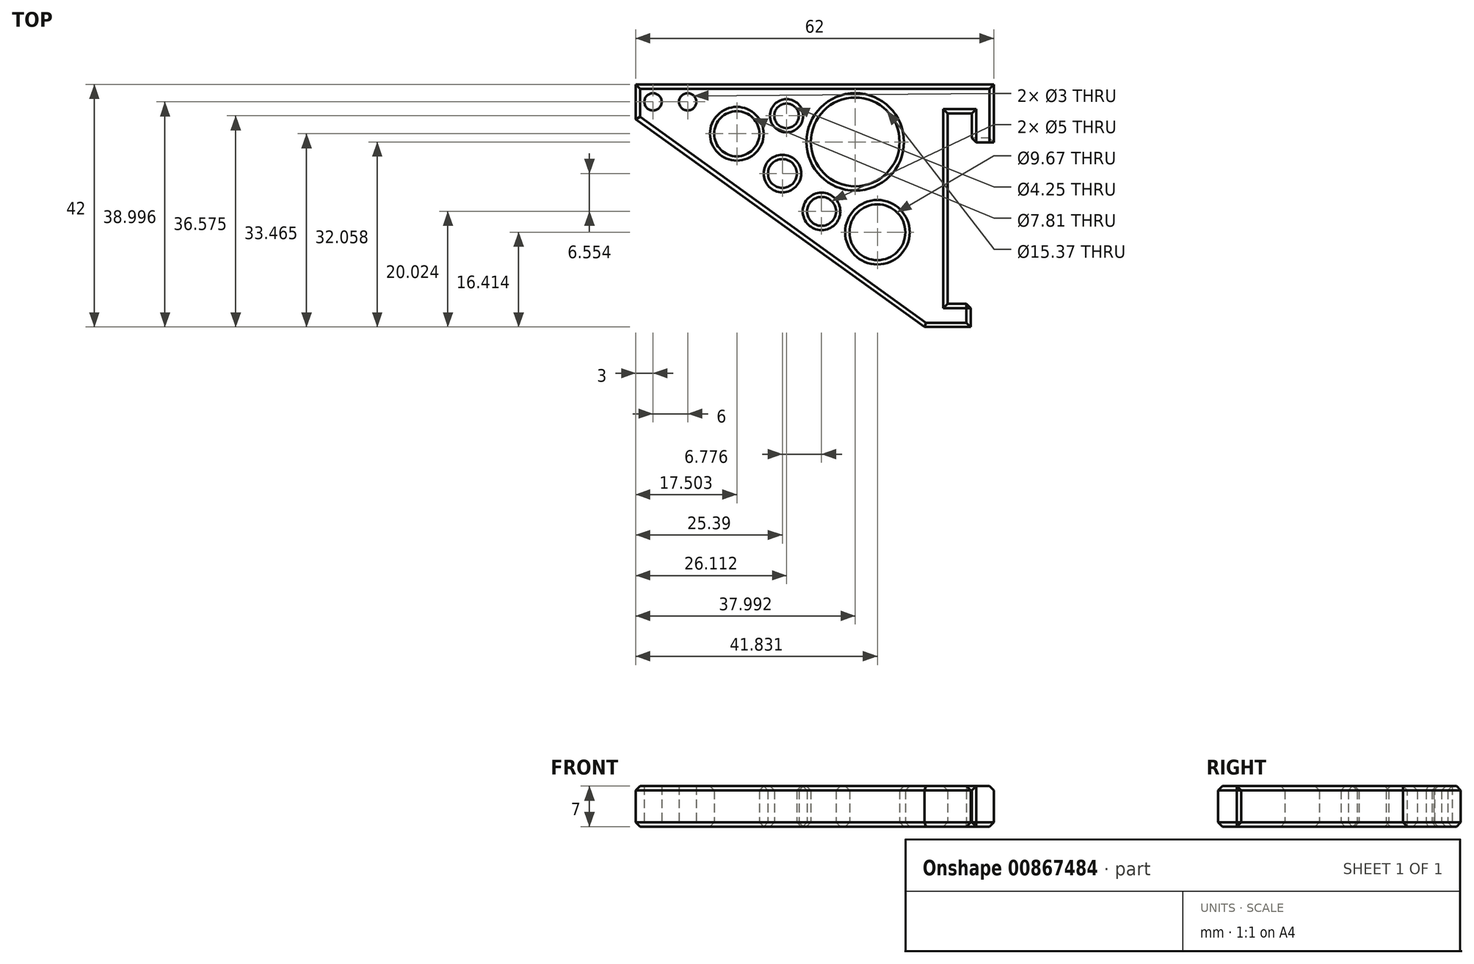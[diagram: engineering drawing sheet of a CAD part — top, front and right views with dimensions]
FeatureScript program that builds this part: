
annotation { "Feature Type Name" : "Feature", "Feature Type Description" : "" }
export const myFeature = defineFeature(function(context is Context, id is Id, definition is map)
    precondition{}
    {
        {
            var Q0;
            Q0=qCreatedBy(makeId("Top.planeOp"),FACE);
            var sketch = newSketch(context, id + "F0", { "sketchPlane" : qUnion([Q0])});
            skLineSegment(sketch, "E0.bottom", {"start": v(0, 15.63) * mm, "end": v(-4, 15.63) * mm});
            skLineSegment(sketch, "E0.top", {"start": v(0, -26.37) * mm, "end": v(-4, -26.37) * mm});
            skLineSegment(sketch, "E0.left", {"start": v(0, 15.63) * mm, "end": v(0, -26.37) * mm});
            skLineSegment(sketch, "E1.bottom", {"start": v(0, 15.63) * mm, "end": v(8, 15.63) * mm});
            skLineSegment(sketch, "E1.top", {"start": v(0, 10.63) * mm, "end": v(8, 10.63) * mm});
            skLineSegment(sketch, "E1.left", {"start": v(0, 15.63) * mm, "end": v(0, 10.63) * mm});
            skLineSegment(sketch, "E1.right", {"start": v(8, 15.63) * mm, "end": v(8, 10.63) * mm});
            skLineSegment(sketch, "E2.bottom", {"start": v(8, 10.63) * mm, "end": v(4.2, 10.63) * mm});
            skLineSegment(sketch, "E2.top", {"start": v(8, 5.63) * mm, "end": v(4.2, 5.63) * mm});
            skLineSegment(sketch, "E2.left", {"start": v(8, 10.63) * mm, "end": v(8, 5.63) * mm});
            skLineSegment(sketch, "E2.right", {"start": v(4.2, 10.63) * mm, "end": v(4.2, 5.63) * mm});
            skLineSegment(sketch, "E3.bottom", {"start": v(0, -26.37) * mm, "end": v(4, -26.37) * mm});
            skLineSegment(sketch, "E3.top", {"start": v(0, -22.37) * mm, "end": v(4, -22.37) * mm});
            skLineSegment(sketch, "E3.left", {"start": v(0, -26.37) * mm, "end": v(0, -22.37) * mm});
            skLineSegment(sketch, "E3.right", {"start": v(4, -26.37) * mm, "end": v(4, -22.37) * mm});
            skLineSegment(sketch, "E4", {"start": v(-4, 15.63) * mm, "end": v(-4, -26.37) * mm});
            skLineSegment(sketch, "E5", {"start": v(-4, 15.63) * mm, "end": v(-54, 15.63) * mm});
            skLineSegment(sketch, "E6", {"start": v(-54, 15.63) * mm, "end": v(-54, 9.63) * mm});
            skLineSegment(sketch, "E7", {"start": v(-54, 9.63) * mm, "end": v(-4, -26.37) * mm});
            skCircle(sketch, "E8", {"center": v(-16, 5.69) * mm, "radius": 7.68 * mm});
            skCircle(sketch, "E9", {"center": v(-36.5, 7.1) * mm, "radius": 3.9 * mm});
            skCircle(sketch, "E10", {"center": v(-27.89, 10.2) * mm, "radius": 2.12 * mm});
            skCircle(sketch, "E11", {"center": v(-28.6, 0.2) * mm, "radius": 2.5 * mm});
            skCircle(sketch, "E12", {"center": v(-12.17, -9.96) * mm, "radius": 4.83 * mm});
            skLineSegment(sketch, "E13.bottom", {"start": v(-54, 15.63) * mm, "end": v(-42, 15.63) * mm});
            skLineSegment(sketch, "E13.top", {"start": v(-54, 9.63) * mm, "end": v(-42, 9.63) * mm});
            skLineSegment(sketch, "E13.right", {"start": v(-42, 15.63) * mm, "end": v(-42, 9.63) * mm});
            skLineSegment(sketch, "E14", {"start": v(-54, 12.63) * mm, "end": v(-51, 12.63) * mm, "construction": true});
            skLineSegment(sketch, "E15", {"start": v(-51, 12.63) * mm, "end": v(-45, 12.63) * mm, "construction": true});
            skLineSegment(sketch, "E16", {"start": v(-45, 12.63) * mm, "end": v(-42, 12.63) * mm, "construction": true});
            skCircle(sketch, "E17", {"center": v(-51, 12.63) * mm, "radius": 1.5 * mm});
            skCircle(sketch, "E18", {"center": v(-45, 12.63) * mm, "radius": 1.5 * mm});
            skCircle(sketch, "E19", {"center": v(-21.83, -6.35) * mm, "radius": 2.5 * mm});
            skSolve(sketch);
        }
        {
            var Q0;
            {var subQ1=sQuery(id+"F0.wireOp",EDGE,"E0.bottom");Q0=makeQuery(id+"F0.imprint","IMPRINT",FACE,{"disambiguationData":[TD([[makeQuery(id+"F0.imprint","IMPRINT",EDGE,{"derivedFrom":subQ1}),1.0]])]});}
            var Q1;
            {var subQ4=sQuery(id+"F0.wireOp",EDGE,"E1.bottom");Q1=makeQuery(id+"F0.imprint","IMPRINT",FACE,{"disambiguationData":[TD([[makeQuery(id+"F0.imprint","IMPRINT",EDGE,{"derivedFrom":subQ4}),-1.0]])]});}
            var Q2;
            Q2=makeQuery(id+"F0.imprint","IMPRINT",FACE,{"disambiguationData":[TD([[makeQuery(id+"F0.imprint","IMPRINT",EDGE,{"derivedFrom":sQuery(id+"F0.wireOp",EDGE,"E2.top")}),-1.0]])]});
            var Q3;
            {var subQ0=sQuery(id+"F0.wireOp",EDGE,"E3.bottom");Q3=makeQuery(id+"F0.imprint","IMPRINT",FACE,{"disambiguationData":[TD([[makeQuery(id+"F0.imprint","IMPRINT",EDGE,{"derivedFrom":subQ0}),1.0]])]});}
            var Q4;
            {var subQ0=sQuery(id+"F0.wireOp",EDGE,"E4");Q4=makeQuery(id+"F0.imprint","IMPRINT",FACE,{"disambiguationData":[TD([[makeQuery(id+"F0.imprint","IMPRINT",EDGE,{"derivedFrom":subQ0}),-1.0]])]});}
            var Q5;
            {var subQ0=sQuery(id+"F0.wireOp",EDGE,"E6");Q5=makeQuery(id+"F0.imprint","IMPRINT",FACE,{"disambiguationData":[TD([[makeQuery(id+"F0.imprint","IMPRINT",EDGE,{"derivedFrom":subQ0}),1.0]])]});}
            extrude(context, id + "F1", {"entities" : qUnion([Q0, Q1, Q2, Q3, Q4, Q5]), "depth" : 7 * mm, "offsetDistance" : 25 * mm});
        }
        {
            var Q0;
            Q0=makeQuery(id+"F1.opExtrude","SWEPT_EDGE",EDGE,{"disambiguationData":[OSD([sQuery(id+"F0.wireOp",EDGE,"E2.top"),sQuery(id+"F0.wireOp",EDGE,"E2.right")])]});
            var Q1;
            Q1=makeQuery(id+"F1.opExtrude","SWEPT_EDGE",EDGE,{"disambiguationData":[OSD([sQuery(id+"F0.wireOp",EDGE,"E3.top"),sQuery(id+"F0.wireOp",EDGE,"E3.right")])]});
            var Q2;
            Q2=makeQuery(id+"F1.opExtrude","CAP_EDGE",EDGE,{"disambiguationData":[OSD([sQuery(id+"F0.wireOp",EDGE,"uG2Vx7Yd-SFKq-mX41-H8Db-6Rk8HB1i1w4M")])],"isStart":true});
            var Q3;
            Q3=makeQuery(id+"F1.opExtrude","CAP_EDGE",EDGE,{"disambiguationData":[OSD([sQuery(id+"F0.wireOp",EDGE,"uG2Vx7Yd-SFKq-mX41-H8Db-6Rk8HB1i1w4M")])],"isStart":false});
            var Q4;
            Q4=makeQuery(id+"F1.opExtrude","CAP_EDGE",EDGE,{"disambiguationData":[OSD([sQuery(id+"F0.wireOp",EDGE,"E12")])],"isStart":true});
            var Q5;
            Q5=makeQuery(id+"F1.opExtrude","CAP_EDGE",EDGE,{"disambiguationData":[OSD([sQuery(id+"F0.wireOp",EDGE,"oTn9qpCm-4VPc-hakh-BUWp-S5fq27Ghi3sC")])],"isStart":true});
            var Q6;
            Q6=makeQuery(id+"F1.opExtrude","CAP_EDGE",EDGE,{"disambiguationData":[OSD([sQuery(id+"F0.wireOp",EDGE,"eH2JkWFH-rGqj-qHwk-75RG-LBSng5KapZW2")])],"isStart":true});
            var Q7;
            Q7=makeQuery(id+"F1.opExtrude","CAP_EDGE",EDGE,{"disambiguationData":[OSD([sQuery(id+"F0.wireOp",EDGE,"WzFQYJBc-jEeU-135c-dLvn-cKav0WjsmrNZ")])],"isStart":true});
            var Q8;
            Q8=makeQuery(id+"F1.opExtrude","CAP_EDGE",EDGE,{"disambiguationData":[OSD([sQuery(id+"F0.wireOp",EDGE,"E11")])],"isStart":true});
            var Q9;
            Q9=makeQuery(id+"F1.opExtrude","CAP_EDGE",EDGE,{"disambiguationData":[OSD([sQuery(id+"F0.wireOp",EDGE,"E9")])],"isStart":false});
            var Q10;
            Q10=makeQuery(id+"F1.opExtrude","CAP_EDGE",EDGE,{"disambiguationData":[OSD([sQuery(id+"F0.wireOp",EDGE,"E9")])],"isStart":true});
            var Q11;
            Q11=makeQuery(id+"F1.opExtrude","CAP_EDGE",EDGE,{"disambiguationData":[OSD([sQuery(id+"F0.wireOp",EDGE,"E10")])],"isStart":true});
            var Q12;
            Q12=makeQuery(id+"F1.opExtrude","CAP_EDGE",EDGE,{"disambiguationData":[OSD([sQuery(id+"F0.wireOp",EDGE,"E8")])],"isStart":true});
            var Q13;
            Q13=makeQuery(id+"F1.opExtrude","CAP_EDGE",EDGE,{"disambiguationData":[OSD([sQuery(id+"F0.wireOp",EDGE,"E0.left")])],"isStart":true});
            var Q14;
            Q14=makeQuery(id+"F1.opExtrude","CAP_EDGE",EDGE,{"disambiguationData":[OSD([sQuery(id+"F0.wireOp",EDGE,"E1.top")])],"isStart":true});
            var Q15;
            Q15=makeQuery(id+"F1.opExtrude","CAP_EDGE",EDGE,{"disambiguationData":[OSD([sQuery(id+"F0.wireOp",EDGE,"E2.right")])],"isStart":true});
            var Q16;
            Q16=makeQuery(id+"F1.opExtrude","CAP_EDGE",EDGE,{"disambiguationData":[OSD([sQuery(id+"F0.wireOp",EDGE,"E2.top")])],"isStart":true});
            var Q17;
            Q17=makeQuery(id+"F1.opExtrude","CAP_EDGE",EDGE,{"disambiguationData":[OSD([sQuery(id+"F0.wireOp",EDGE,"E1.right"),sQuery(id+"F0.wireOp",EDGE,"E2.left")])],"isStart":true});
            var Q18;
            Q18=makeQuery(id+"F1.opExtrude","CAP_EDGE",EDGE,{"disambiguationData":[OSD([sQuery(id+"F0.wireOp",EDGE,"E0.bottom"),sQuery(id+"F0.wireOp",EDGE,"E1.bottom"),sQuery(id+"F0.wireOp",EDGE,"E5")])],"isStart":true});
            var Q19;
            Q19=makeQuery(id+"F1.opExtrude","CAP_EDGE",EDGE,{"disambiguationData":[OSD([sQuery(id+"F0.wireOp",EDGE,"E6")])],"isStart":true});
            var Q20;
            Q20=makeQuery(id+"F1.opExtrude","CAP_EDGE",EDGE,{"disambiguationData":[OSD([sQuery(id+"F0.wireOp",EDGE,"E7")])],"isStart":true});
            var Q21;
            Q21=makeQuery(id+"F1.opExtrude","CAP_EDGE",EDGE,{"disambiguationData":[OSD([sQuery(id+"F0.wireOp",EDGE,"E0.top"),sQuery(id+"F0.wireOp",EDGE,"E3.bottom")])],"isStart":true});
            var Q22;
            Q22=makeQuery(id+"F1.opExtrude","CAP_EDGE",EDGE,{"disambiguationData":[OSD([sQuery(id+"F0.wireOp",EDGE,"E3.right")])],"isStart":true});
            var Q23;
            Q23=makeQuery(id+"F1.opExtrude","CAP_EDGE",EDGE,{"disambiguationData":[OSD([sQuery(id+"F0.wireOp",EDGE,"E3.top")])],"isStart":true});
            var Q24;
            Q24=makeQuery(id+"F1.opExtrude","CAP_EDGE",EDGE,{"disambiguationData":[OSD([sQuery(id+"F0.wireOp",EDGE,"E0.bottom"),sQuery(id+"F0.wireOp",EDGE,"E1.bottom"),sQuery(id+"F0.wireOp",EDGE,"E5")])],"isStart":false});
            var Q25;
            Q25=makeQuery(id+"F1.opExtrude","CAP_EDGE",EDGE,{"disambiguationData":[OSD([sQuery(id+"F0.wireOp",EDGE,"E6")])],"isStart":false});
            var Q26;
            Q26=makeQuery(id+"F1.opExtrude","CAP_EDGE",EDGE,{"disambiguationData":[OSD([sQuery(id+"F0.wireOp",EDGE,"E7")])],"isStart":false});
            var Q27;
            Q27=makeQuery(id+"F1.opExtrude","CAP_EDGE",EDGE,{"disambiguationData":[OSD([sQuery(id+"F0.wireOp",EDGE,"E10")])],"isStart":false});
            var Q28;
            Q28=makeQuery(id+"F1.opExtrude","CAP_EDGE",EDGE,{"disambiguationData":[OSD([sQuery(id+"F0.wireOp",EDGE,"E11")])],"isStart":false});
            var Q29;
            Q29=makeQuery(id+"F1.opExtrude","CAP_EDGE",EDGE,{"disambiguationData":[OSD([sQuery(id+"F0.wireOp",EDGE,"E8")])],"isStart":false});
            var Q30;
            Q30=makeQuery(id+"F1.opExtrude","CAP_EDGE",EDGE,{"disambiguationData":[OSD([sQuery(id+"F0.wireOp",EDGE,"WzFQYJBc-jEeU-135c-dLvn-cKav0WjsmrNZ")])],"isStart":false});
            var Q31;
            Q31=makeQuery(id+"F1.opExtrude","CAP_EDGE",EDGE,{"disambiguationData":[OSD([sQuery(id+"F0.wireOp",EDGE,"E12")])],"isStart":false});
            var Q32;
            Q32=makeQuery(id+"F1.opExtrude","CAP_EDGE",EDGE,{"disambiguationData":[OSD([sQuery(id+"F0.wireOp",EDGE,"eH2JkWFH-rGqj-qHwk-75RG-LBSng5KapZW2")])],"isStart":false});
            var Q33;
            Q33=makeQuery(id+"F1.opExtrude","CAP_EDGE",EDGE,{"disambiguationData":[OSD([sQuery(id+"F0.wireOp",EDGE,"oTn9qpCm-4VPc-hakh-BUWp-S5fq27Ghi3sC")])],"isStart":false});
            var Q34;
            Q34=makeQuery(id+"F1.opExtrude","CAP_EDGE",EDGE,{"disambiguationData":[OSD([sQuery(id+"F0.wireOp",EDGE,"E0.top"),sQuery(id+"F0.wireOp",EDGE,"E3.bottom")])],"isStart":false});
            var Q35;
            Q35=makeQuery(id+"F1.opExtrude","CAP_EDGE",EDGE,{"disambiguationData":[OSD([sQuery(id+"F0.wireOp",EDGE,"E3.right")])],"isStart":false});
            var Q36;
            Q36=makeQuery(id+"F1.opExtrude","CAP_EDGE",EDGE,{"disambiguationData":[OSD([sQuery(id+"F0.wireOp",EDGE,"E3.top")])],"isStart":false});
            var Q37;
            Q37=makeQuery(id+"F1.opExtrude","CAP_EDGE",EDGE,{"disambiguationData":[OSD([sQuery(id+"F0.wireOp",EDGE,"E0.left")])],"isStart":false});
            var Q38;
            Q38=makeQuery(id+"F1.opExtrude","CAP_EDGE",EDGE,{"disambiguationData":[OSD([sQuery(id+"F0.wireOp",EDGE,"E1.right"),sQuery(id+"F0.wireOp",EDGE,"E2.left")])],"isStart":false});
            var Q39;
            Q39=makeQuery(id+"F1.opExtrude","CAP_EDGE",EDGE,{"disambiguationData":[OSD([sQuery(id+"F0.wireOp",EDGE,"E1.top")])],"isStart":false});
            var Q40;
            Q40=makeQuery(id+"F1.opExtrude","CAP_EDGE",EDGE,{"disambiguationData":[OSD([sQuery(id+"F0.wireOp",EDGE,"E2.right")])],"isStart":false});
            var Q41;
            Q41=makeQuery(id+"F1.opExtrude","CAP_EDGE",EDGE,{"disambiguationData":[OSD([sQuery(id+"F0.wireOp",EDGE,"E19")])],"isStart":false});
            var Q42;
            Q42=makeQuery(id+"F1.opExtrude","CAP_EDGE",EDGE,{"disambiguationData":[OSD([sQuery(id+"F0.wireOp",EDGE,"E19")])],"isStart":true});
            chamfer(context, id + "F2", {"entities" : qUnion([Q0, Q1, Q2, Q3, Q4, Q5, Q6, Q7, Q8, Q9, Q10, Q11, Q12, Q13, Q14, Q15, Q16, Q17, Q18, Q19, Q20, Q21, Q22, Q23, Q24, Q25, Q26, Q27, Q28, Q29, Q30, Q31, Q32, Q33, Q34, Q35, Q36, Q37, Q38, Q39, Q40, Q41, Q42]), "width" : 0.75 * mm, "tangentPropagation" : true});
        }
    });
